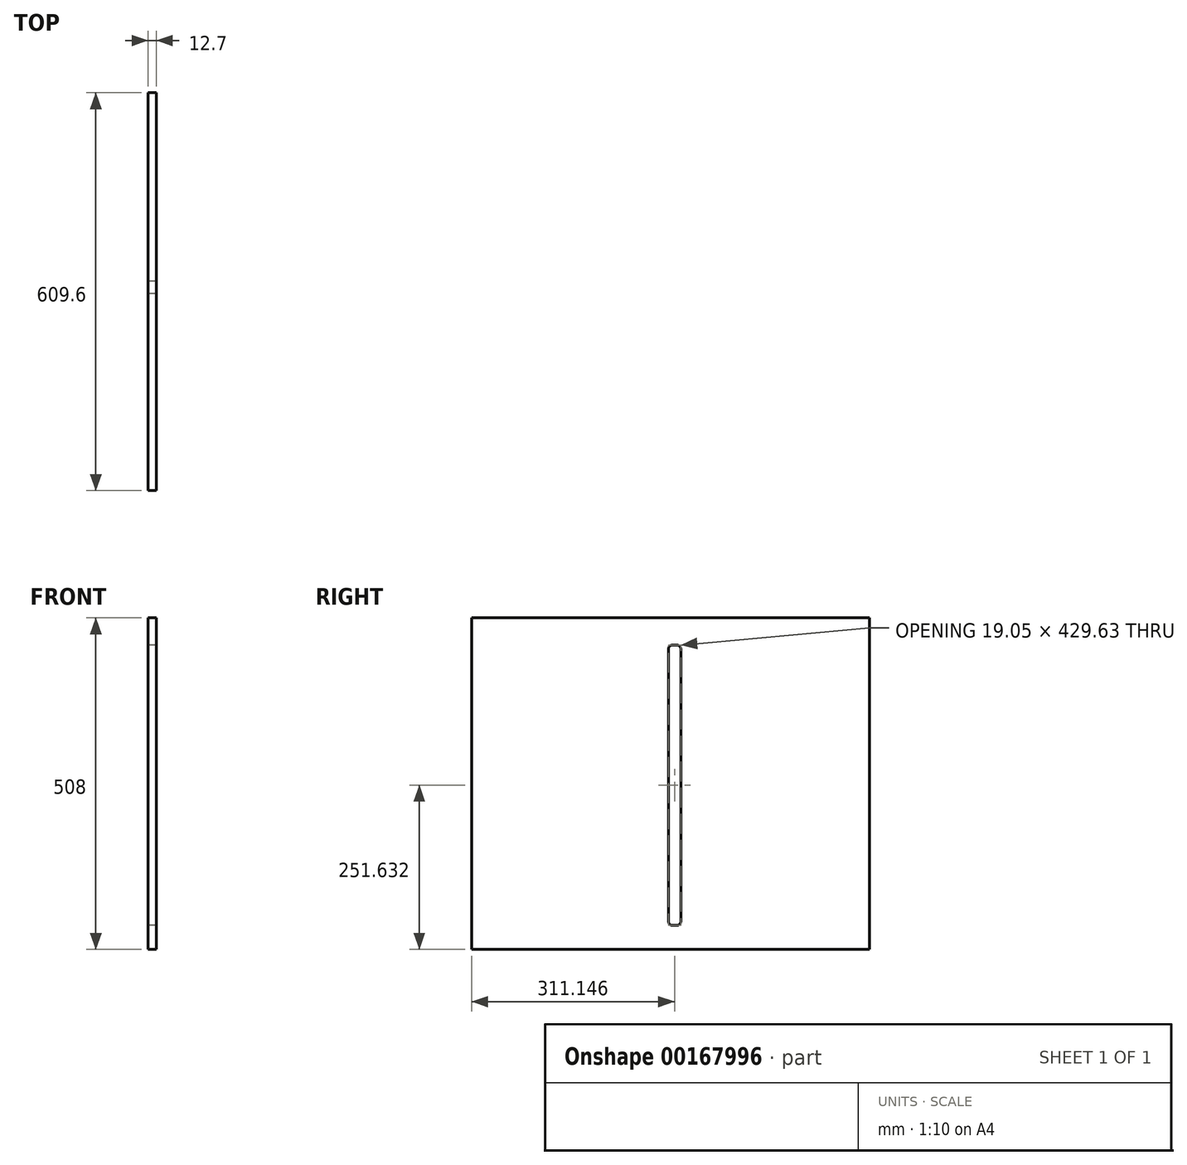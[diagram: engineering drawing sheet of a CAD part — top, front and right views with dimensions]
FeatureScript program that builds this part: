
annotation { "Feature Type Name" : "Feature", "Feature Type Description" : "" }
export const myFeature = defineFeature(function(context is Context, id is Id, definition is map)
    precondition{}
    {
        {
            var Q0;
            Q0=qCreatedBy(makeId("Right.planeOp"),FACE);
            var sketch = newSketch(context, id + "F0", { "sketchPlane" : qUnion([Q0])});
            skLineSegment(sketch, "E0.bottom", {"start": v(-48.16, 508) * mm, "end": v(561.44, 508) * mm});
            skLineSegment(sketch, "E0.top", {"start": v(-48.16, 0) * mm, "end": v(561.44, 0) * mm});
            skLineSegment(sketch, "E0.left", {"start": v(-48.16, 508) * mm, "end": v(-48.16, 0) * mm});
            skLineSegment(sketch, "E0.right", {"start": v(561.44, 508) * mm, "end": v(561.44, 0) * mm});
            skLineSegment(sketch, "E1.bottom", {"start": v(259.81, 466.45) * mm, "end": v(266.16, 466.45) * mm});
            skLineSegment(sketch, "E1.top", {"start": v(259.81, 36.82) * mm, "end": v(266.16, 36.82) * mm});
            skLineSegment(sketch, "E1.left", {"start": v(253.46, 460.1) * mm, "end": v(253.46, 43.17) * mm});
            skLineSegment(sketch, "E1.right", {"start": v(272.51, 460.1) * mm, "end": v(272.51, 43.17) * mm});
            skPoint(sketch, "E2.visualSharp", {"position": v(253.46, 466.45) * mm});
            skArc(sketch, "E2.filletArc", {"start": v(259.81, 466.45) * mm, "mid": v(255.32, 464.59) * mm, "end": v(253.46, 460.1) * mm});
            skPoint(sketch, "E3.visualSharp", {"position": v(272.51, 466.45) * mm});
            skArc(sketch, "E3.filletArc", {"start": v(272.51, 460.1) * mm, "mid": v(270.65, 464.59) * mm, "end": v(266.16, 466.45) * mm});
            skPoint(sketch, "E4.visualSharp", {"position": v(272.51, 36.82) * mm});
            skArc(sketch, "E4.filletArc", {"start": v(266.16, 36.82) * mm, "mid": v(270.65, 38.68) * mm, "end": v(272.51, 43.17) * mm});
            skPoint(sketch, "E5.visualSharp", {"position": v(253.46, 36.82) * mm});
            skArc(sketch, "E5.filletArc", {"start": v(253.46, 43.17) * mm, "mid": v(255.32, 38.68) * mm, "end": v(259.81, 36.82) * mm});
            skSolve(sketch);
        }
        {
            var Q0;
            Q0=makeQuery(id+"F0.imprint","IMPRINT",FACE,{"disambiguationData":[TD([[makeQuery(id+"F0.imprint","IMPRINT",EDGE,{"derivedFrom":sQuery(id+"F0.wireOp",EDGE,"E0.bottom")}),-1.0]])]});
            extrude(context, id + "F1", {"entities" : qUnion([Q0]), "depth" : 12.7 * mm});
        }
    });
